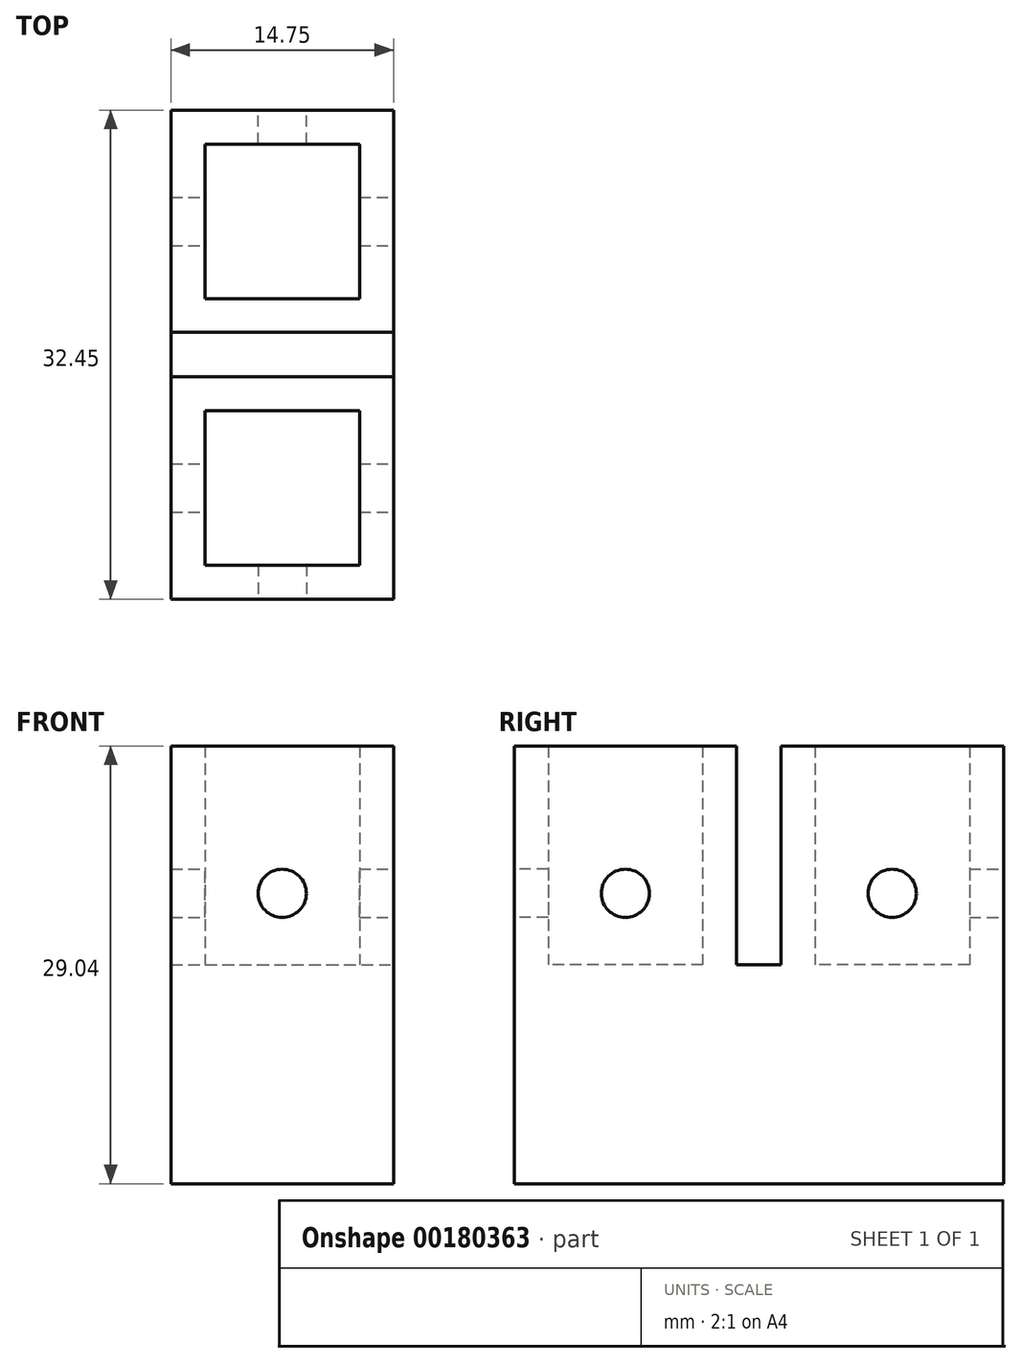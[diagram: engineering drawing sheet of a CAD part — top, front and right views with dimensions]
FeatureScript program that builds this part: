
annotation { "Feature Type Name" : "Feature", "Feature Type Description" : "" }
export const myFeature = defineFeature(function(context is Context, id is Id, definition is map)
    precondition{}
    {
        {
            var Q0;
            Q0=qCreatedBy(makeId("Top.planeOp"),FACE);
            var sketch = newSketch(context, id + "F0", { "sketchPlane" : qUnion([Q0])});
            skLineSegment(sketch, "E0.bottom", {"start": v(0, 0) * mm, "end": v(10.25, 0) * mm});
            skLineSegment(sketch, "E0.top", {"start": v(0, -10.25) * mm, "end": v(10.25, -10.25) * mm});
            skLineSegment(sketch, "E0.left", {"start": v(0, 0) * mm, "end": v(0, -10.25) * mm});
            skLineSegment(sketch, "E0.right", {"start": v(10.25, 0) * mm, "end": v(10.25, -10.25) * mm});
            skLineSegment(sketch, "E1.bottom", {"start": v(-2.25, 2.25) * mm, "end": v(12.5, 2.25) * mm});
            skLineSegment(sketch, "E1.top", {"start": v(-2.25, -12.5) * mm, "end": v(12.5, -12.5) * mm});
            skLineSegment(sketch, "E1.left", {"start": v(-2.25, 2.25) * mm, "end": v(-2.25, -12.5) * mm});
            skLineSegment(sketch, "E1.right", {"start": v(12.5, 2.25) * mm, "end": v(12.5, -12.5) * mm});
            skSolve(sketch);
        }
        {
            var Q0;
            Q0=makeQuery(id+"F0.imprint","IMPRINT",FACE,{"disambiguationData":[TD([[makeQuery(id+"F0.imprint","IMPRINT",EDGE,{"derivedFrom":sQuery(id+"F0.wireOp",EDGE,"E0.bottom")}),1.0]])]});
            extrude(context, id + "F1", {"entities" : qUnion([Q0]), "depth" : 14.52 * mm});
        }
        {
            var Q0;
            Q0=makeQuery(id+"F1.opExtrude","CAP_FACE",FACE,{"disambiguationData":[OSD([sQuery(id+"F0.wireOp",EDGE,"E0.bottom"),sQuery(id+"F0.wireOp",EDGE,"E0.top"),sQuery(id+"F0.wireOp",EDGE,"E0.left"),sQuery(id+"F0.wireOp",EDGE,"E0.right"),sQuery(id+"F0.wireOp",EDGE,"E1.bottom"),sQuery(id+"F0.wireOp",EDGE,"E1.top"),sQuery(id+"F0.wireOp",EDGE,"E1.left"),sQuery(id+"F0.wireOp",EDGE,"E1.right")])],"isStart":true});
            var sketch = newSketch(context, id + "F2", { "sketchPlane" : qUnion([Q0])});
            skLineSegment(sketch, "E2.bottom", {"start": v(-2.25, -2.25) * mm, "end": v(12.5, -2.25) * mm});
            skLineSegment(sketch, "E2.top", {"start": v(-2.25, 12.5) * mm, "end": v(12.5, 12.5) * mm});
            skLineSegment(sketch, "E2.left", {"start": v(-2.25, -2.25) * mm, "end": v(-2.25, 12.5) * mm});
            skLineSegment(sketch, "E2.right", {"start": v(12.5, -2.25) * mm, "end": v(12.5, 12.5) * mm});
            skLineSegment(sketch, "E3.left", {"start": v(-2.25, 12.5) * mm, "end": v(-2.25, -2.25) * mm});
            skLineSegment(sketch, "E3.right", {"start": v(12.5, 12.5) * mm, "end": v(12.5, -2.25) * mm});
            skSolve(sketch);
        }
        {
            var Q0;
            Q0=makeQuery(id+"F2.imprint","IMPRINT",FACE,{"disambiguationData":[TD([[makeQuery(id+"F2.imprint","IMPRINT",EDGE,{"derivedFrom":sQuery(id+"F2.wireOp",EDGE,"E2.top")}),-1.0]])]});
            var Q1;
            Q1=makeQuery(id+"F2.imprint","IMPRINT",FACE,{"disambiguationData":[TD([[makeQuery(id+"F2.imprint","IMPRINT",EDGE,{"derivedFrom":makeQuery(id+"F1.opExtrude","CAP_EDGE",EDGE,{"disambiguationData":[OSD([sQuery(id+"F0.wireOp",EDGE,"E0.bottom")])],"isStart":true})}),1.0]])]});
            extrude(context, id + "F3", {"entities" : qUnion([Q0, Q1]), "operationType" : NewBodyOperationType.ADD, "depth" : 14.52 * mm});
        }
        {
            var Q0;
            Q0=makeQuery(id+"F3.boolean.opBoolean","MERGE",FACE,{"derivedFrom":[makeQuery(id+"F1.opExtrude","SWEPT_FACE",FACE,{"disambiguationData":[OSD([sQuery(id+"F0.wireOp",EDGE,"E1.top")])]}),makeQuery(id+"F3.opExtrude","SWEPT_FACE",FACE,{"disambiguationData":[OSD([sQuery(id+"F2.wireOp",EDGE,"E2.top")])]})]});
            var sketch = newSketch(context, id + "F4", { "sketchPlane" : qUnion([Q0])});
            skLineSegment(sketch, "E4.bottom", {"start": v(-2.25, 0) * mm, "end": v(12.5, 0) * mm});
            skLineSegment(sketch, "E4.top", {"start": v(-2.25, -14.52) * mm, "end": v(12.5, -14.52) * mm});
            skLineSegment(sketch, "E4.left", {"start": v(-2.25, 0) * mm, "end": v(-2.25, -14.52) * mm});
            skLineSegment(sketch, "E4.right", {"start": v(12.5, 0) * mm, "end": v(12.5, -14.52) * mm});
            skLineSegment(sketch, "E5.left", {"start": v(0, -2.25) * mm, "end": v(0, -12.27) * mm});
            skLineSegment(sketch, "E5.right", {"start": v(10.25, -2.25) * mm, "end": v(10.25, -12.27) * mm});
            skLineSegment(sketch, "E6.bottom", {"start": v(0, -2.25) * mm, "end": v(10.25, -2.25) * mm});
            skLineSegment(sketch, "E6.top", {"start": v(0, -12.5) * mm, "end": v(10.25, -12.5) * mm});
            skLineSegment(sketch, "E6.left", {"start": v(0, -2.25) * mm, "end": v(0, -12.5) * mm});
            skLineSegment(sketch, "E6.right", {"start": v(10.25, -2.25) * mm, "end": v(10.25, -12.5) * mm});
            skSolve(sketch);
        }
        {
            var Q0;
            Q0=makeQuery(id+"F4.imprint","IMPRINT",FACE,{"disambiguationData":[TD([[makeQuery(id+"F4.imprint","IMPRINT",EDGE,{"derivedFrom":sQuery(id+"F4.wireOp",EDGE,"E4.bottom")}),-1.0]])]});
            var sketch = newSketch(context, id + "F5", { "sketchPlane" : qUnion([Q0])});
            skLineSegment(sketch, "E7.0.0", {"start": v(12.5, 0) * mm, "end": v(-2.25, 0) * mm});
            skLineSegment(sketch, "E7.0.1", {"start": v(-2.25, 0) * mm, "end": v(-2.25, -14.52) * mm});
            skLineSegment(sketch, "E7.0.2", {"start": v(-2.25, -14.52) * mm, "end": v(12.5, -14.52) * mm});
            skLineSegment(sketch, "E7.0.3", {"start": v(12.5, -14.52) * mm, "end": v(12.5, 0) * mm});
            skSolve(sketch);
        }
        {
            var Q0;
            Q0 = qSketchRegion(id + "F5", true);
            var Q1;
            Q1=makeQuery(id+"F4.imprint","IMPRINT",FACE,{"disambiguationData":[TD([[makeQuery(id+"F4.imprint","IMPRINT",EDGE,{"derivedFrom":sQuery(id+"F4.wireOp",EDGE,"E4.bottom")}),-1.0]])]});
            var Q2;
            {var subQ3=sQuery(id+"F4.wireOp",EDGE,"E6.bottom");Q2=makeQuery(id+"F4.imprint","IMPRINT",FACE,{"disambiguationData":[TD([[makeQuery(id+"F4.imprint","IMPRINT",EDGE,{"derivedFrom":subQ3}),-1.0]])]});}
            extrude(context, id + "F6", {"entities" : qUnion([Q0, Q1, Q2]), "operationType" : NewBodyOperationType.ADD, "depth" : 17.7 * mm});
        }
        {
            var Q0;
            Q0=makeQuery(id+"F6.opExtrude","SWEPT_FACE",FACE,{"disambiguationData":[OSD([sQuery(id+"F4.wireOp",EDGE,"E4.bottom")])]});
            var sketch = newSketch(context, id + "F7", { "sketchPlane" : qUnion([Q0])});
            skLineSegment(sketch, "E8.bottom", {"start": v(0, -17.7) * mm, "end": v(10.25, -17.7) * mm});
            skLineSegment(sketch, "E8.top", {"start": v(0, -27.95) * mm, "end": v(10.25, -27.95) * mm});
            skLineSegment(sketch, "E8.left", {"start": v(0, -17.7) * mm, "end": v(0, -27.95) * mm});
            skLineSegment(sketch, "E8.right", {"start": v(10.25, -17.7) * mm, "end": v(10.25, -27.95) * mm});
            skLineSegment(sketch, "E9.bottom", {"start": v(-2.25, -15.45) * mm, "end": v(12.5, -15.45) * mm});
            skLineSegment(sketch, "E9.top", {"start": v(-2.25, -30.2) * mm, "end": v(12.5, -30.2) * mm});
            skLineSegment(sketch, "E9.left", {"start": v(-2.25, -15.45) * mm, "end": v(-2.25, -30.2) * mm});
            skLineSegment(sketch, "E9.right", {"start": v(12.5, -15.45) * mm, "end": v(12.5, -30.2) * mm});
            skSolve(sketch);
        }
        {
            var Q0;
            Q0=makeQuery(id+"F7.imprint","IMPRINT",FACE,{"disambiguationData":[TD([[makeQuery(id+"F7.imprint","IMPRINT",EDGE,{"derivedFrom":sQuery(id+"F7.wireOp",EDGE,"E8.bottom")}),1.0]])]});
            extrude(context, id + "F8", {"entities" : qUnion([Q0]), "operationType" : NewBodyOperationType.ADD, "depth" : 14.52 * mm});
        }
        {
            var Q0;
            Q0=makeQuery(id+"F8.boolean.opBoolean","MERGE",FACE,{"derivedFrom":[makeQuery(id+"F6.boolean.opBoolean","MERGE",FACE,{"derivedFrom":[makeQuery(id+"F3.boolean.opBoolean","MERGE",FACE,{"derivedFrom":[makeQuery(id+"F1.opExtrude","SWEPT_FACE",FACE,{"disambiguationData":[OSD([sQuery(id+"F0.wireOp",EDGE,"E1.right")])]}),makeQuery(id+"F3.opExtrude","SWEPT_FACE",FACE,{"disambiguationData":[OSD([sQuery(id+"F2.wireOp",EDGE,"E3.right")])]})]}),makeQuery(id+"F6.opExtrude","SWEPT_FACE",FACE,{"disambiguationData":[OSD([sQuery(id+"F4.wireOp",EDGE,"E4.right")])]})]}),makeQuery(id+"F8.opExtrude","SWEPT_FACE",FACE,{"disambiguationData":[OSD([sQuery(id+"F7.wireOp",EDGE,"E9.right")])]})]});
            var sketch = newSketch(context, id + "F9", { "sketchPlane" : qUnion([Q0])});
            skLineSegment(sketch, "E10.0.0", {"start": v(-12.5, 14.52) * mm, "end": v(-12.5, 0) * mm});
            skLineSegment(sketch, "E10.0.1", {"start": v(-12.5, 0) * mm, "end": v(-15.45, 0) * mm});
            skLineSegment(sketch, "E10.0.2", {"start": v(-15.45, 0) * mm, "end": v(-15.45, 14.52) * mm});
            skLineSegment(sketch, "E10.0.3", {"start": v(-15.45, 14.52) * mm, "end": v(-30.2, 14.52) * mm});
            skLineSegment(sketch, "E10.0.4", {"start": v(-30.2, 14.52) * mm, "end": v(-30.2, -14.52) * mm});
            skLineSegment(sketch, "E10.0.5", {"start": v(-30.2, -14.52) * mm, "end": v(2.25, -14.52) * mm});
            skLineSegment(sketch, "E10.0.6", {"start": v(2.25, -14.52) * mm, "end": v(2.25, 14.52) * mm});
            skLineSegment(sketch, "E10.0.7", {"start": v(2.25, 14.52) * mm, "end": v(-12.5, 14.52) * mm});
            skCircle(sketch, "E11", {"center": v(-22.82, 4.75) * mm, "radius": 1.6 * mm});
            skPoint(sketch, "E11.centerSnap0", {"position": v(-22.82, 14.52) * mm});
            skPoint(sketch, "E11.centerSnap1", {"position": v(-15.45, 4.75) * mm});
            skCircle(sketch, "E12", {"center": v(-5.12, 4.75) * mm, "radius": 1.6 * mm});
            skPoint(sketch, "E12.centerSnap0", {"position": v(-5.12, 14.52) * mm});
            skLineSegment(sketch, "E13.0.0", {"start": v(-27.95, 0) * mm, "end": v(-17.7, 0) * mm});
            skLineSegment(sketch, "E13.0.1", {"start": v(-17.7, 0) * mm, "end": v(-17.7, 14.52) * mm});
            skLineSegment(sketch, "E13.0.2", {"start": v(-17.7, 14.52) * mm, "end": v(-27.95, 14.52) * mm});
            skLineSegment(sketch, "E13.0.3", {"start": v(-27.95, 14.52) * mm, "end": v(-27.95, 0) * mm});
            skLineSegment(sketch, "E14.0.0", {"start": v(-10.25, 0) * mm, "end": v(0, 0) * mm});
            skLineSegment(sketch, "E14.0.1", {"start": v(0, 0) * mm, "end": v(0, 14.52) * mm});
            skLineSegment(sketch, "E14.0.2", {"start": v(0, 14.52) * mm, "end": v(-10.25, 14.52) * mm});
            skLineSegment(sketch, "E14.0.3", {"start": v(-10.25, 14.52) * mm, "end": v(-10.25, 0) * mm});
            skSolve(sketch);
        }
        {
            var Q0;
            Q0=makeQuery(id+"F9.imprint","IMPRINT",FACE,{"disambiguationData":[TD([[makeQuery(id+"F9.imprint","IMPRINT",EDGE,{"derivedFrom":sQuery(id+"F9.wireOp",EDGE,"E11")}),1.0]])]});
            var Q1;
            Q1=makeQuery(id+"F9.imprint","IMPRINT",FACE,{"disambiguationData":[TD([[makeQuery(id+"F9.imprint","IMPRINT",EDGE,{"derivedFrom":sQuery(id+"F9.wireOp",EDGE,"E12")}),1.0]])]});
            extrude(context, id + "F10", {"entities" : qUnion([Q0, Q1]), "operationType" : NewBodyOperationType.REMOVE, "oppositeDirection" : true, "depth" : 25.4 * mm});
        }
        {
            var Q0;
            Q0=makeQuery(id+"F8.boolean.opBoolean","MERGE",FACE,{"derivedFrom":[makeQuery(id+"F6.opExtrude","CAP_FACE",FACE,{"disambiguationData":[OSD([sQuery(id+"F4.wireOp",EDGE,"E4.bottom"),sQuery(id+"F4.wireOp",EDGE,"E4.top"),sQuery(id+"F4.wireOp",EDGE,"E4.left"),sQuery(id+"F4.wireOp",EDGE,"E4.right")])],"isStart":false}),makeQuery(id+"F8.opExtrude","SWEPT_FACE",FACE,{"disambiguationData":[OSD([sQuery(id+"F7.wireOp",EDGE,"E9.top")])]})]});
            var sketch = newSketch(context, id + "F11", { "sketchPlane" : qUnion([Q0])});
            skCircle(sketch, "E15", {"center": v(5.13, 4.75) * mm, "radius": 1.6 * mm});
            skPoint(sketch, "E15.centerSnap0", {"position": v(5.13, 14.52) * mm});
            skLineSegment(sketch, "E16.0.0", {"start": v(0, 0) * mm, "end": v(10.25, 0) * mm});
            skLineSegment(sketch, "E16.0.1", {"start": v(10.25, 0) * mm, "end": v(10.25, 14.52) * mm});
            skLineSegment(sketch, "E16.0.2", {"start": v(10.25, 14.52) * mm, "end": v(0, 14.52) * mm});
            skLineSegment(sketch, "E16.0.3", {"start": v(0, 14.52) * mm, "end": v(0, 0) * mm});
            skSolve(sketch);
        }
        {
            var Q0;
            Q0=makeQuery(id+"F11.imprint","IMPRINT",FACE,{"disambiguationData":[TD([[makeQuery(id+"F11.imprint","IMPRINT",EDGE,{"derivedFrom":sQuery(id+"F11.wireOp",EDGE,"E15")}),1.0]])]});
            extrude(context, id + "F12", {"entities" : qUnion([Q0]), "operationType" : NewBodyOperationType.REMOVE, "oppositeDirection" : true, "depth" : 10 * mm});
        }
        {
            var Q0;
            Q0=makeQuery(id+"F3.boolean.opBoolean","MERGE",FACE,{"derivedFrom":[makeQuery(id+"F1.opExtrude","SWEPT_FACE",FACE,{"disambiguationData":[OSD([sQuery(id+"F0.wireOp",EDGE,"E1.bottom")])]}),makeQuery(id+"F3.opExtrude","SWEPT_FACE",FACE,{"disambiguationData":[OSD([sQuery(id+"F2.wireOp",EDGE,"E2.bottom")])]})]});
            var sketch = newSketch(context, id + "F13", { "sketchPlane" : qUnion([Q0])});
            skLineSegment(sketch, "E17.0.0", {"start": v(-10.25, 0) * mm, "end": v(0, 0) * mm});
            skLineSegment(sketch, "E17.0.1", {"start": v(0, 0) * mm, "end": v(0, 14.52) * mm});
            skLineSegment(sketch, "E17.0.2", {"start": v(0, 14.52) * mm, "end": v(-10.25, 14.52) * mm});
            skLineSegment(sketch, "E17.0.3", {"start": v(-10.25, 14.52) * mm, "end": v(-10.25, 0) * mm});
            skCircle(sketch, "E18.0", {"center": v(-5.13, 4.75) * mm, "radius": 1.6 * mm});
            skSolve(sketch);
        }
        {
            var Q0;
            Q0=makeQuery(id+"F13.imprint","IMPRINT",FACE,{"disambiguationData":[TD([[makeQuery(id+"F13.imprint","IMPRINT",EDGE,{"derivedFrom":sQuery(id+"F13.wireOp",EDGE,"E18.0")}),1.0]])]});
            extrude(context, id + "F14", {"entities" : qUnion([Q0]), "operationType" : NewBodyOperationType.REMOVE, "oppositeDirection" : true, "depth" : 10 * mm});
        }
    });
